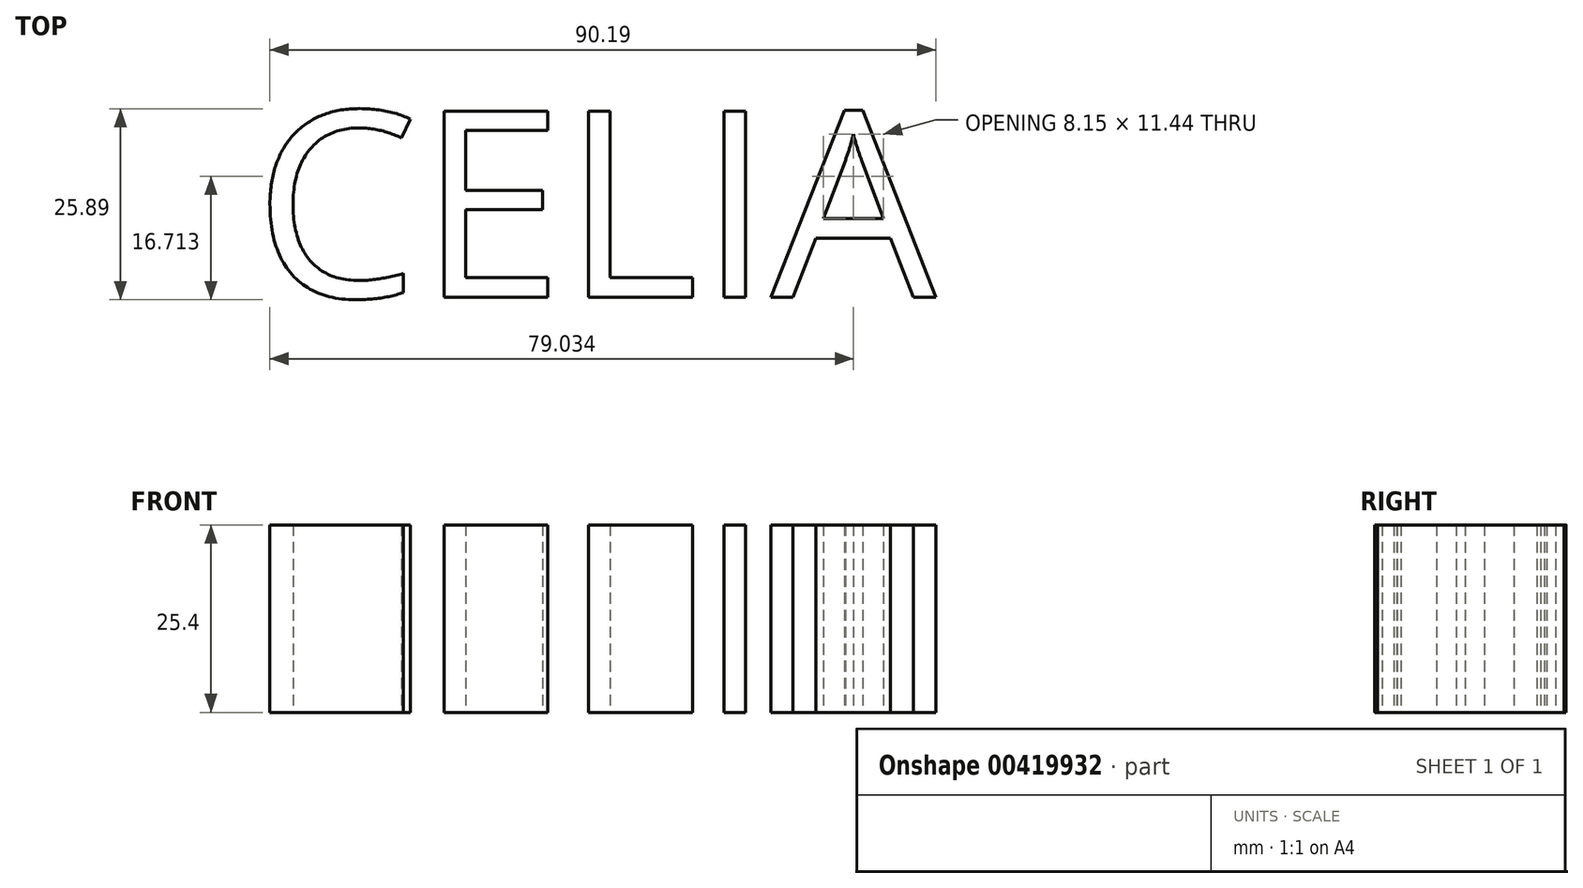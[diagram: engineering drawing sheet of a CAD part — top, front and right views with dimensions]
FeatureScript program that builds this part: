
annotation { "Feature Type Name" : "Feature", "Feature Type Description" : "" }
export const myFeature = defineFeature(function(context is Context, id is Id, definition is map)
    precondition{}
    {
        {
            var Q0;
            Q0=qCreatedBy(makeId("Top.planeOp"),FACE);
            var sketch = newSketch(context, id + "F0", { "sketchPlane" : qUnion([Q0])});
            skText(sketch, "E0", { "text": "CELIA", "fontName": "OpenSans-Regular.ttf"});
            const initialGuessF0  = {"E0": [-0.02428, -0.00828, 1, 0, 0.0254]};
            skSetInitialGuess(sketch, initialGuessF0);
            skSolve(sketch);
        }
        {
            var Q0;
            Q0 = qSketchRegion(id + "F0", true);
            extrude(context, id + "F1", {"entities" : qUnion([Q0]), "depth" : 25.4 * mm});
        }
    });
